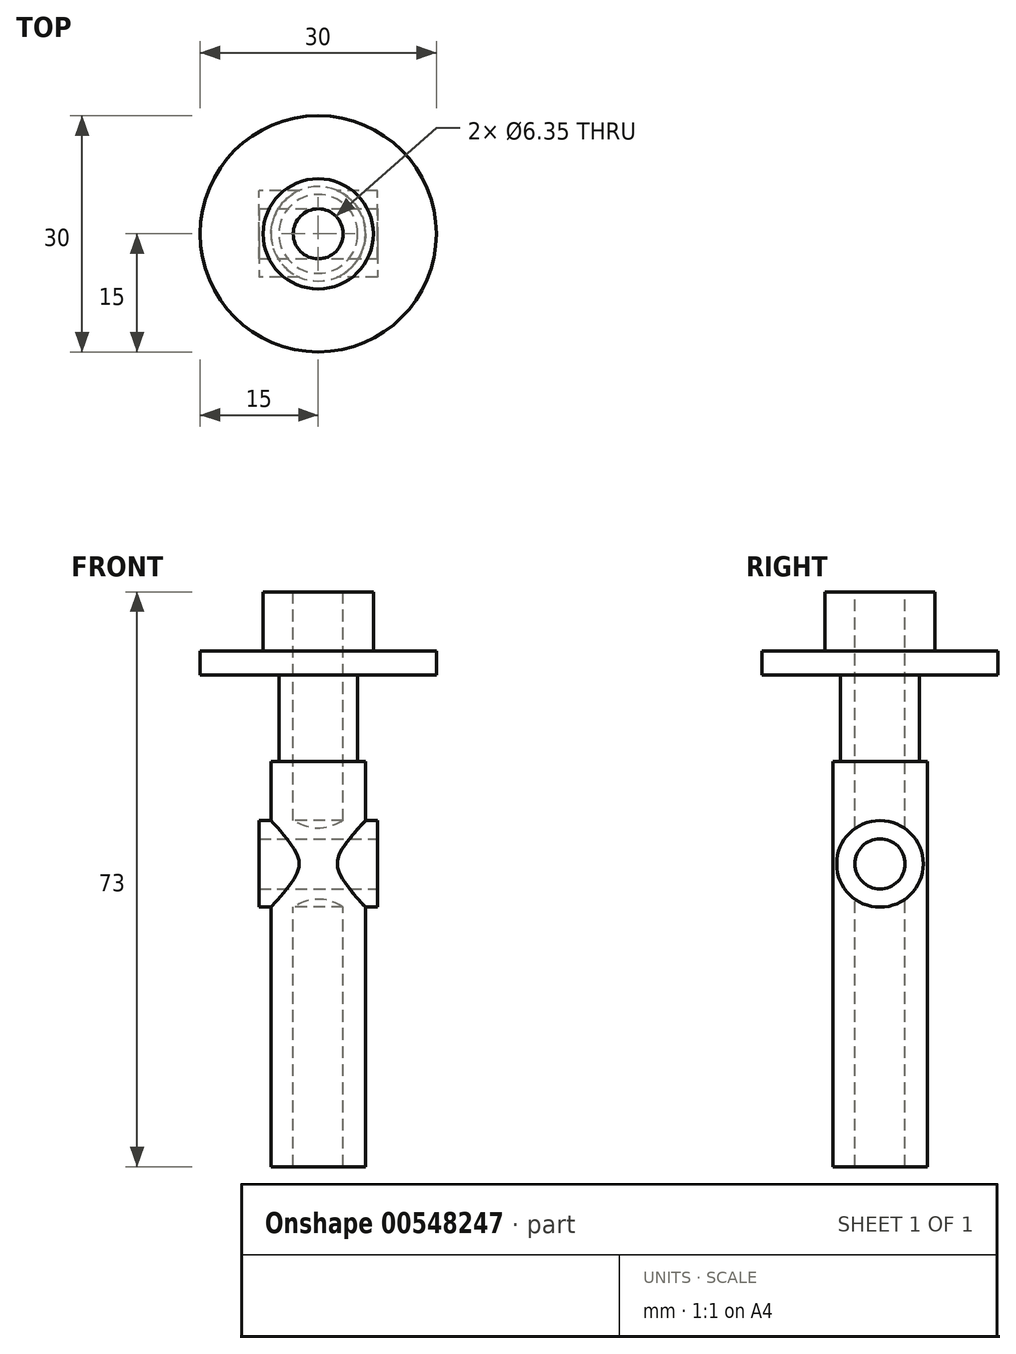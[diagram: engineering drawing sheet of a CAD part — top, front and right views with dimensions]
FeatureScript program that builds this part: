
annotation { "Feature Type Name" : "Feature", "Feature Type Description" : "" }
export const myFeature = defineFeature(function(context is Context, id is Id, definition is map)
    precondition{}
    {
        {
            var Q0;
            Q0=qCreatedBy(makeId("Right.planeOp"),FACE);
            var sketch = newSketch(context, id + "F0", { "sketchPlane" : qUnion([Q0])});
            skLineSegment(sketch, "E0", {"start": v(0, -35.94) * mm, "end": v(0, 37.06) * mm});
            skLineSegment(sketch, "E1", {"start": v(0, 37.06) * mm, "end": v(7, 37.06) * mm});
            skLineSegment(sketch, "E2", {"start": v(7, 37.06) * mm, "end": v(7, 29.58) * mm});
            skLineSegment(sketch, "E3", {"start": v(7, 29.58) * mm, "end": v(15, 29.58) * mm});
            skLineSegment(sketch, "E4", {"start": v(15, 29.58) * mm, "end": v(15, 26.53) * mm});
            skLineSegment(sketch, "E5", {"start": v(15, 26.53) * mm, "end": v(5, 26.53) * mm});
            skLineSegment(sketch, "E6", {"start": v(5, 26.53) * mm, "end": v(5, 15.53) * mm});
            skLineSegment(sketch, "E7", {"start": v(5, 15.53) * mm, "end": v(6, 15.53) * mm});
            skLineSegment(sketch, "E8", {"start": v(6, 15.53) * mm, "end": v(6, -35.94) * mm});
            skLineSegment(sketch, "E9", {"start": v(6, -35.94) * mm, "end": v(0, -35.94) * mm});
            skSolve(sketch);
        }
        {
            var Q0;
            Q0 = qSketchRegion(id + "F0", true);
            var Q1;
            Q1=sQuery(id+"F0.wireOp",EDGE,"E0");
            revolve(context, id + "F1", {"entities" : qUnion([Q0]), "axis" : qUnion([Q1]), "revolveType" : RevolveType.FULL});
        }
        {
            var Q0;
            Q0=makeQuery(id+"F1.opRevolve","SWEPT_FACE",FACE,{"disambiguationData":[OSD([sQuery(id+"F0.wireOp",EDGE,"E1")])]});
            var sketch = newSketch(context, id + "F2", { "sketchPlane" : qUnion([Q0])});
            skPoint(sketch, "E10", {"position": v(0, 0) * mm});
            skSolve(sketch);
        }
        {
            var Q0;
            Q0=sQuery(id+"F2.wireOp",VERTEX,"E10");
            var Q1;
            Q1=makeQuery(id+"F1.opRevolve","SWEPT_BODY",BODY,{"disambiguationData":[OSD([sQuery(id+"F0.wireOp",EDGE,"E0"),sQuery(id+"F0.wireOp",EDGE,"E1"),sQuery(id+"F0.wireOp",EDGE,"E2"),sQuery(id+"F0.wireOp",EDGE,"E3"),sQuery(id+"F0.wireOp",EDGE,"E4"),sQuery(id+"F0.wireOp",EDGE,"E5"),sQuery(id+"F0.wireOp",EDGE,"E6"),sQuery(id+"F0.wireOp",EDGE,"E7"),sQuery(id+"F0.wireOp",EDGE,"E8"),sQuery(id+"F0.wireOp",EDGE,"E9")])]});
            hole(context, id + "F3", {"style" : HoleStyle.SIMPLE, "endStyle" : HoleEndStyle.THROUGH, "holeDiameter" : 6.35 * mm, "isTappedThrough" : true, "tappedDepth" : 12 * mm, "tapClearance" : 3, "locations" : qUnion([Q0]), "scope" : qUnion([Q1])});
        }
        {
            var Q0;
            Q0=qCreatedBy(makeId("Right.planeOp"),FACE);
            var sketch = newSketch(context, id + "F4", { "sketchPlane" : qUnion([Q0])});
            skCircle(sketch, "E11", {"center": v(0, 2.53) * mm, "radius": 5.5 * mm});
            skLineSegment(sketch, "E12.0", {"start": v(6, 15.53) * mm, "end": v(-6, 15.53) * mm});
            skSolve(sketch);
        }
        {
            var Q0;
            Q0 = qSketchRegion(id + "F4", true);
            extrude(context, id + "F5", {"entities" : qUnion([Q0]), "operationType" : NewBodyOperationType.ADD, "endBound" : BoundingType.SYMMETRIC, "depth" : 15 * mm, "offsetDistance" : 25 * mm});
        }
        {
            var Q0;
            Q0=makeQuery(id+"F5.opExtrude","CAP_FACE",FACE,{"disambiguationData":[OSD([sQuery(id+"F4.wireOp",EDGE,"E11")])],"isStart":false});
            var sketch = newSketch(context, id + "F6", { "sketchPlane" : qUnion([Q0])});
            skPoint(sketch, "E13", {"position": v(0, 2.53) * mm});
            skSolve(sketch);
        }
        {
            var Q0;
            Q0=sQuery(id+"F6.wireOp",VERTEX,"E13");
            var Q1;
            Q1=makeQuery(id+"F1.opRevolve","SWEPT_BODY",BODY,{"disambiguationData":[OSD([sQuery(id+"F0.wireOp",EDGE,"E0"),sQuery(id+"F0.wireOp",EDGE,"E1"),sQuery(id+"F0.wireOp",EDGE,"E2"),sQuery(id+"F0.wireOp",EDGE,"E3"),sQuery(id+"F0.wireOp",EDGE,"E4"),sQuery(id+"F0.wireOp",EDGE,"E5"),sQuery(id+"F0.wireOp",EDGE,"E6"),sQuery(id+"F0.wireOp",EDGE,"E7"),sQuery(id+"F0.wireOp",EDGE,"E8"),sQuery(id+"F0.wireOp",EDGE,"E9")])]});
            hole(context, id + "F7", {"style" : HoleStyle.SIMPLE, "endStyle" : HoleEndStyle.THROUGH, "holeDiameter" : 6.35 * mm, "isTappedThrough" : true, "tappedDepth" : 12 * mm, "tapClearance" : 3, "locations" : qUnion([Q0]), "scope" : qUnion([Q1])});
        }
        {
            var Q0;
            Q0=makeQuery(id+"F1.opRevolve","SWEPT_FACE",FACE,{"disambiguationData":[OSD([sQuery(id+"F0.wireOp",EDGE,"E9")])]});
            var sketch = newSketch(context, id + "F8", { "sketchPlane" : qUnion([Q0])});
            skLineSegment(sketch, "E14", {"start": v(0, 0) * mm, "end": v(0, 10.15) * mm, "construction": true});
            skLineSegment(sketch, "E15", {"start": v(0, 0) * mm, "end": v(3.08, 5.15) * mm, "construction": true});
            skLineSegment(sketch, "E16", {"start": v(0, 0) * mm, "end": v(-3.08, 5.15) * mm, "construction": true});
            skSolve(sketch);
        }
    });
